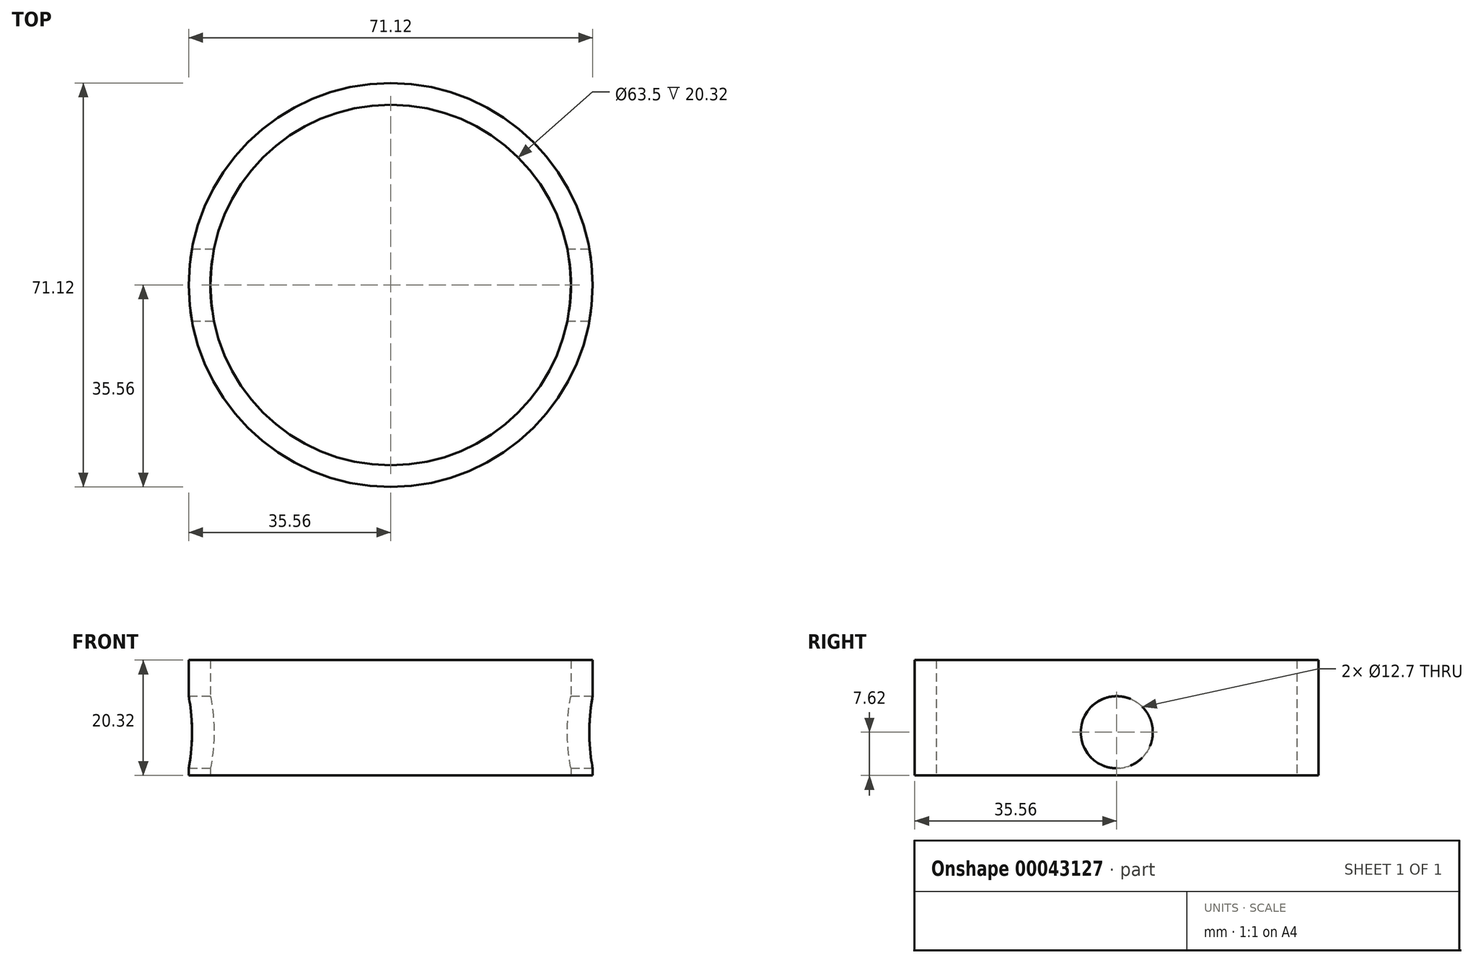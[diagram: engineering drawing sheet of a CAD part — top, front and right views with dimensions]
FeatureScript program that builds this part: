
annotation { "Feature Type Name" : "Feature", "Feature Type Description" : "" }
export const myFeature = defineFeature(function(context is Context, id is Id, definition is map)
    precondition{}
    {
        {
            var Q0;
            Q0=qCreatedBy(makeId("Top.planeOp"),FACE);
            var sketch = newSketch(context, id + "F0", { "sketchPlane" : qUnion([Q0])});
            skCircle(sketch, "E0", {"center": v(0, 0) * mm, "radius": 35.56 * mm});
            skCircle(sketch, "E1", {"center": v(0, 0) * mm, "radius": 31.75 * mm});
            skSolve(sketch);
        }
        {
            var Q0;
            Q0=makeQuery(id+"F0.imprint","IMPRINT",FACE,{"disambiguationData":[TD([[makeQuery(id+"F0.imprint","IMPRINT",EDGE,{"derivedFrom":sQuery(id+"F0.wireOp",EDGE,"E0")}),1.0]])]});
            extrude(context, id + "F1", {"entities" : qUnion([Q0]), "depth" : 20.32 * mm});
        }
        {
            var Q0;
            Q0=qCreatedBy(makeId("Right.planeOp"),FACE);
            var sketch = newSketch(context, id + "F2", { "sketchPlane" : qUnion([Q0])});
            skCircle(sketch, "E2", {"center": v(0, 7.62) * mm, "radius": 6.35 * mm});
            skSolve(sketch);
        }
        {
            var Q0;
            Q0 = qSketchRegion(id + "F2", true);
            extrude(context, id + "F3", {"entities" : qUnion([Q0]), "operationType" : NewBodyOperationType.REMOVE, "oppositeDirection" : true, "depth" : 66.58 * mm, "hasSecondDirection" : true, "secondDirectionOppositeDirection" : false, "secondDirectionDepth" : 53.55 * mm});
        }
    });
